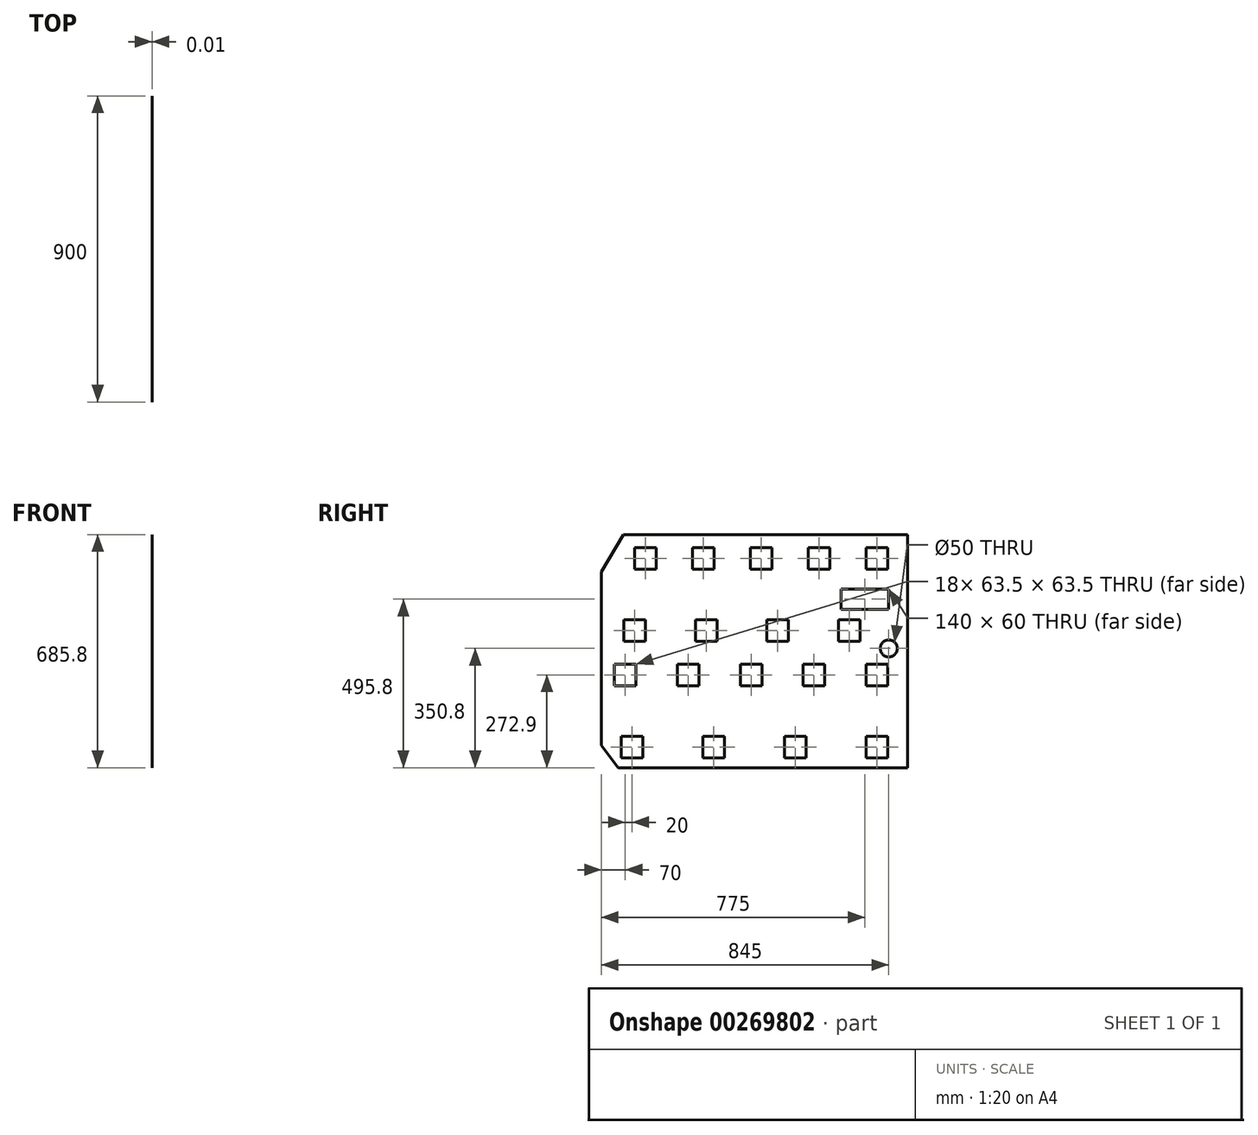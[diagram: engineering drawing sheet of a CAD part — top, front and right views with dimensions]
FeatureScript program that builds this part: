
annotation { "Feature Type Name" : "Feature", "Feature Type Description" : "" }
export const myFeature = defineFeature(function(context is Context, id is Id, definition is map)
    precondition{}
    {
        {
            var Q0;
            Q0=qCreatedBy(makeId("Right.planeOp"),FACE);
            var sketch = newSketch(context, id + "F0", { "sketchPlane" : qUnion([Q0])});
            skLineSegment(sketch, "E0.bottom", {"start": v(450, -342.9) * mm, "end": v(-400, -342.9) * mm});
            skLineSegment(sketch, "E0.top", {"start": v(450, 342.9) * mm, "end": v(-385, 342.9) * mm});
            skLineSegment(sketch, "E0.left", {"start": v(450, -342.9) * mm, "end": v(450, 342.9) * mm});
            skLineSegment(sketch, "E0.right", {"start": v(-450, -277.9) * mm, "end": v(-450, 232.9) * mm});
            skPoint(sketch, "E0.middle", {"position": v(0, 0) * mm});
            skLineSegment(sketch, "E1", {"start": v(-450, -277.9) * mm, "end": v(-400, -342.9) * mm});
            skLineSegment(sketch, "E2", {"start": v(-450, 232.9) * mm, "end": v(-385, 342.9) * mm});
            skLineSegment(sketch, "E3.bottom", {"start": v(395, 122.9) * mm, "end": v(255, 122.9) * mm});
            skLineSegment(sketch, "E3.top", {"start": v(395, 182.9) * mm, "end": v(255, 182.9) * mm});
            skLineSegment(sketch, "E3.left", {"start": v(395, 122.9) * mm, "end": v(395, 182.9) * mm});
            skLineSegment(sketch, "E3.right", {"start": v(255, 122.9) * mm, "end": v(255, 182.9) * mm});
            skPoint(sketch, "E3.middle", {"position": v(325, 152.9) * mm});
            skCircle(sketch, "E4", {"center": v(395, 7.9) * mm, "radius": 25 * mm});
            skPoint(sketch, "E5.orphan", {"position": v(-450, 342.9) * mm});
            skPoint(sketch, "E6.orphan", {"position": v(-450, -342.9) * mm});
            skLineSegment(sketch, "E7", {"start": v(450, 0) * mm, "end": v(-450, 0) * mm, "construction": true});
            skLineSegment(sketch, "E8.bottom", {"start": v(-288.25, 241.15) * mm, "end": v(-351.75, 241.15) * mm});
            skLineSegment(sketch, "E8.top", {"start": v(-288.25, 304.65) * mm, "end": v(-351.75, 304.65) * mm});
            skLineSegment(sketch, "E8.left", {"start": v(-288.25, 241.15) * mm, "end": v(-288.25, 304.65) * mm});
            skLineSegment(sketch, "E8.right", {"start": v(-351.75, 241.15) * mm, "end": v(-351.75, 304.65) * mm});
            skPoint(sketch, "E8.middle", {"position": v(-320, 272.9) * mm});
            skLineSegment(sketch, "E9.1.0.0", {"start": v(-118.25, 241.15) * mm, "end": v(-181.75, 241.15) * mm});
            skLineSegment(sketch, "E9.1.0.1", {"start": v(-181.75, 241.15) * mm, "end": v(-181.75, 304.65) * mm});
            skLineSegment(sketch, "E9.1.0.2", {"start": v(-118.25, 241.15) * mm, "end": v(-118.25, 304.65) * mm});
            skLineSegment(sketch, "E9.1.0.3", {"start": v(-118.25, 304.65) * mm, "end": v(-181.75, 304.65) * mm});
            skPoint(sketch, "E9.1.0.4", {"position": v(-150, 272.9) * mm});
            skLineSegment(sketch, "E9.2.0.0", {"start": v(51.75, 241.15) * mm, "end": v(-11.75, 241.15) * mm});
            skLineSegment(sketch, "E9.2.0.1", {"start": v(-11.75, 241.15) * mm, "end": v(-11.75, 304.65) * mm});
            skLineSegment(sketch, "E9.2.0.2", {"start": v(51.75, 241.15) * mm, "end": v(51.75, 304.65) * mm});
            skLineSegment(sketch, "E9.2.0.3", {"start": v(51.75, 304.65) * mm, "end": v(-11.75, 304.65) * mm});
            skPoint(sketch, "E9.2.0.4", {"position": v(20, 272.9) * mm});
            skLineSegment(sketch, "E9.3.0.0", {"start": v(221.75, 241.15) * mm, "end": v(158.25, 241.15) * mm});
            skLineSegment(sketch, "E9.3.0.1", {"start": v(158.25, 241.15) * mm, "end": v(158.25, 304.65) * mm});
            skLineSegment(sketch, "E9.3.0.2", {"start": v(221.75, 241.15) * mm, "end": v(221.75, 304.65) * mm});
            skLineSegment(sketch, "E9.3.0.3", {"start": v(221.75, 304.65) * mm, "end": v(158.25, 304.65) * mm});
            skPoint(sketch, "E9.3.0.4", {"position": v(190, 272.9) * mm});
            skLineSegment(sketch, "E9.4.0.0", {"start": v(391.75, 241.15) * mm, "end": v(328.25, 241.15) * mm});
            skLineSegment(sketch, "E9.4.0.1", {"start": v(328.25, 241.15) * mm, "end": v(328.25, 304.65) * mm});
            skLineSegment(sketch, "E9.4.0.2", {"start": v(391.75, 241.15) * mm, "end": v(391.75, 304.65) * mm});
            skLineSegment(sketch, "E9.4.0.3", {"start": v(391.75, 304.65) * mm, "end": v(328.25, 304.65) * mm});
            skPoint(sketch, "E9.4.0.4", {"position": v(360, 272.9) * mm});
            skLineSegment(sketch, "E9.direction1", {"start": v(-351.75, 241.15) * mm, "end": v(-181.75, 241.15) * mm, "construction": true});
            skLineSegment(sketch, "E10.bottom", {"start": v(-320, 28.25) * mm, "end": v(-383.5, 28.25) * mm});
            skLineSegment(sketch, "E10.top", {"start": v(-320, 91.75) * mm, "end": v(-383.5, 91.75) * mm});
            skLineSegment(sketch, "E10.left", {"start": v(-320, 28.25) * mm, "end": v(-320, 91.75) * mm});
            skLineSegment(sketch, "E10.right", {"start": v(-383.5, 28.25) * mm, "end": v(-383.5, 91.75) * mm});
            skPoint(sketch, "E10.middle", {"position": v(-351.75, 60) * mm});
            skLineSegment(sketch, "E11.1.0.0", {"start": v(-110, 91.75) * mm, "end": v(-173.5, 91.75) * mm});
            skLineSegment(sketch, "E11.1.0.1", {"start": v(-173.5, 28.25) * mm, "end": v(-173.5, 91.75) * mm});
            skLineSegment(sketch, "E11.1.0.2", {"start": v(-110, 28.25) * mm, "end": v(-110, 91.75) * mm});
            skLineSegment(sketch, "E11.1.0.3", {"start": v(-110, 28.25) * mm, "end": v(-173.5, 28.25) * mm});
            skPoint(sketch, "E11.1.0.4", {"position": v(-141.75, 60) * mm});
            skLineSegment(sketch, "E11.2.0.0", {"start": v(100, 91.75) * mm, "end": v(36.5, 91.75) * mm});
            skLineSegment(sketch, "E11.2.0.1", {"start": v(36.5, 28.25) * mm, "end": v(36.5, 91.75) * mm});
            skLineSegment(sketch, "E11.2.0.2", {"start": v(100, 28.25) * mm, "end": v(100, 91.75) * mm});
            skLineSegment(sketch, "E11.2.0.3", {"start": v(100, 28.25) * mm, "end": v(36.5, 28.25) * mm});
            skPoint(sketch, "E11.2.0.4", {"position": v(68.25, 60) * mm});
            skLineSegment(sketch, "E11.3.0.0", {"start": v(310, 91.75) * mm, "end": v(246.5, 91.75) * mm});
            skLineSegment(sketch, "E11.3.0.1", {"start": v(246.5, 28.25) * mm, "end": v(246.5, 91.75) * mm});
            skLineSegment(sketch, "E11.3.0.2", {"start": v(310, 28.25) * mm, "end": v(310, 91.75) * mm});
            skLineSegment(sketch, "E11.3.0.3", {"start": v(310, 28.25) * mm, "end": v(246.5, 28.25) * mm});
            skPoint(sketch, "E11.3.0.4", {"position": v(278.25, 60) * mm});
            skLineSegment(sketch, "E11.direction1", {"start": v(-383.5, 28.25) * mm, "end": v(-173.5, 28.25) * mm, "construction": true});
            skLineSegment(sketch, "E12.bottom", {"start": v(-348.25, -101.75) * mm, "end": v(-411.75, -101.75) * mm});
            skLineSegment(sketch, "E12.top", {"start": v(-348.25, -38.25) * mm, "end": v(-411.75, -38.25) * mm});
            skLineSegment(sketch, "E12.left", {"start": v(-348.25, -101.75) * mm, "end": v(-348.25, -38.25) * mm});
            skLineSegment(sketch, "E12.right", {"start": v(-411.75, -101.75) * mm, "end": v(-411.75, -38.25) * mm});
            skPoint(sketch, "E12.middle", {"position": v(-380, -70) * mm});
            skLineSegment(sketch, "E13.1.0.0", {"start": v(-163.25, -38.25) * mm, "end": v(-226.75, -38.25) * mm});
            skLineSegment(sketch, "E13.1.0.1", {"start": v(-226.75, -101.75) * mm, "end": v(-226.75, -38.25) * mm});
            skLineSegment(sketch, "E13.1.0.2", {"start": v(-163.25, -101.75) * mm, "end": v(-163.25, -38.25) * mm});
            skPoint(sketch, "E13.1.0.3", {"position": v(-195, -70) * mm});
            skLineSegment(sketch, "E13.1.0.4", {"start": v(-163.25, -101.75) * mm, "end": v(-226.75, -101.75) * mm});
            skLineSegment(sketch, "E13.2.0.0", {"start": v(21.75, -38.25) * mm, "end": v(-41.75, -38.25) * mm});
            skLineSegment(sketch, "E13.2.0.1", {"start": v(-41.75, -101.75) * mm, "end": v(-41.75, -38.25) * mm});
            skLineSegment(sketch, "E13.2.0.2", {"start": v(21.75, -101.75) * mm, "end": v(21.75, -38.25) * mm});
            skPoint(sketch, "E13.2.0.3", {"position": v(-10, -70) * mm});
            skLineSegment(sketch, "E13.2.0.4", {"start": v(21.75, -101.75) * mm, "end": v(-41.75, -101.75) * mm});
            skLineSegment(sketch, "E13.3.0.0", {"start": v(206.75, -38.25) * mm, "end": v(143.25, -38.25) * mm});
            skLineSegment(sketch, "E13.3.0.1", {"start": v(143.25, -101.75) * mm, "end": v(143.25, -38.25) * mm});
            skLineSegment(sketch, "E13.3.0.2", {"start": v(206.75, -101.75) * mm, "end": v(206.75, -38.25) * mm});
            skPoint(sketch, "E13.3.0.3", {"position": v(175, -70) * mm});
            skLineSegment(sketch, "E13.3.0.4", {"start": v(206.75, -101.75) * mm, "end": v(143.25, -101.75) * mm});
            skLineSegment(sketch, "E13.4.0.0", {"start": v(391.75, -38.25) * mm, "end": v(328.25, -38.25) * mm});
            skLineSegment(sketch, "E13.4.0.1", {"start": v(328.25, -101.75) * mm, "end": v(328.25, -38.25) * mm});
            skLineSegment(sketch, "E13.4.0.2", {"start": v(391.75, -101.75) * mm, "end": v(391.75, -38.25) * mm});
            skPoint(sketch, "E13.4.0.3", {"position": v(360, -70) * mm});
            skLineSegment(sketch, "E13.4.0.4", {"start": v(391.75, -101.75) * mm, "end": v(328.25, -101.75) * mm});
            skLineSegment(sketch, "E13.direction1", {"start": v(-411.75, -101.75) * mm, "end": v(-226.75, -101.75) * mm, "construction": true});
            skLineSegment(sketch, "E14.bottom", {"start": v(-328.25, -314.65) * mm, "end": v(-391.75, -314.65) * mm});
            skLineSegment(sketch, "E14.top", {"start": v(-328.25, -251.15) * mm, "end": v(-391.75, -251.15) * mm});
            skLineSegment(sketch, "E14.left", {"start": v(-328.25, -314.65) * mm, "end": v(-328.25, -251.15) * mm});
            skLineSegment(sketch, "E14.right", {"start": v(-391.75, -314.65) * mm, "end": v(-391.75, -251.15) * mm});
            skPoint(sketch, "E14.middle", {"position": v(-360, -282.9) * mm});
            skPoint(sketch, "E15.1.0.0", {"position": v(-120, -282.9) * mm});
            skLineSegment(sketch, "E15.1.0.1", {"start": v(-88.25, -314.65) * mm, "end": v(-151.75, -314.65) * mm});
            skLineSegment(sketch, "E15.1.0.2", {"start": v(-88.25, -251.15) * mm, "end": v(-151.75, -251.15) * mm});
            skLineSegment(sketch, "E15.1.0.3", {"start": v(-88.25, -314.65) * mm, "end": v(-88.25, -251.15) * mm});
            skLineSegment(sketch, "E15.1.0.4", {"start": v(-151.75, -314.65) * mm, "end": v(-151.75, -251.15) * mm});
            skPoint(sketch, "E15.2.0.0", {"position": v(120, -282.9) * mm});
            skLineSegment(sketch, "E15.2.0.1", {"start": v(151.75, -314.65) * mm, "end": v(88.25, -314.65) * mm});
            skLineSegment(sketch, "E15.2.0.2", {"start": v(151.75, -251.15) * mm, "end": v(88.25, -251.15) * mm});
            skLineSegment(sketch, "E15.2.0.3", {"start": v(151.75, -314.65) * mm, "end": v(151.75, -251.15) * mm});
            skLineSegment(sketch, "E15.2.0.4", {"start": v(88.25, -314.65) * mm, "end": v(88.25, -251.15) * mm});
            skPoint(sketch, "E15.3.0.0", {"position": v(360, -282.9) * mm});
            skLineSegment(sketch, "E15.3.0.1", {"start": v(391.75, -314.65) * mm, "end": v(328.25, -314.65) * mm});
            skLineSegment(sketch, "E15.3.0.2", {"start": v(391.75, -251.15) * mm, "end": v(328.25, -251.15) * mm});
            skLineSegment(sketch, "E15.3.0.3", {"start": v(391.75, -314.65) * mm, "end": v(391.75, -251.15) * mm});
            skLineSegment(sketch, "E15.3.0.4", {"start": v(328.25, -314.65) * mm, "end": v(328.25, -251.15) * mm});
            skLineSegment(sketch, "E15.direction1", {"start": v(-391.75, -314.65) * mm, "end": v(-151.75, -314.65) * mm, "construction": true});
            skSolve(sketch);
        }
        {
            var Q0;
            Q0=makeQuery(id+"F0.imprint","IMPRINT",FACE,{"disambiguationData":[TD([[makeQuery(id+"F0.imprint","IMPRINT",EDGE,{"derivedFrom":sQuery(id+"F0.wireOp",EDGE,"E0.bottom")}),-1.0]])]});
            extrude(context, id + "F1", {"entities" : qUnion([Q0]), "depth" : 1 / 101.6 * mm});
        }
    });
